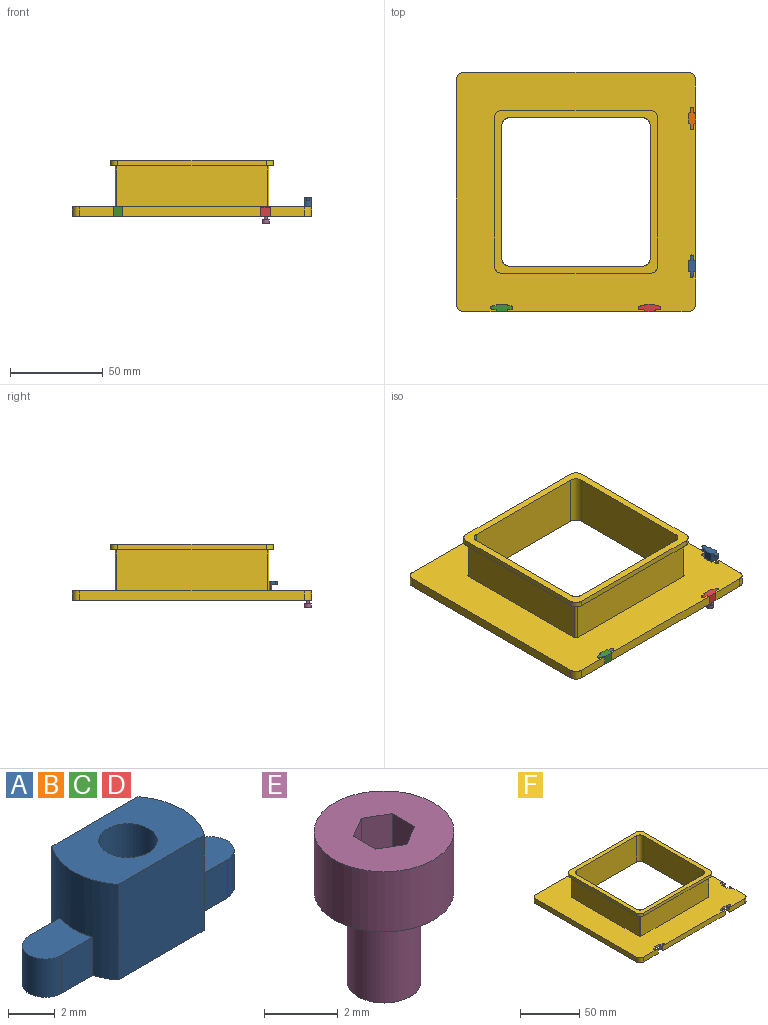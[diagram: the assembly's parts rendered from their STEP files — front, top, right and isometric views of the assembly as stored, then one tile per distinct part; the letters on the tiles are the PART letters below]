
ASSEMBLY  parts=6 mates=5
PART A: 16 faces, bbox 12x4x5 mm
  f0: plane 2x1.88mm, normal (0,1,0), area 3.8mm2, adj f2,f3,f8,f9
  f1: plane 2x1.88mm, normal (0,-1,0), area 3.8mm2, adj f2,f3,f8,f9
  f2: plane 2.88x2mm, normal (0,0,1), area 5.1mm2, adj f0,f1,f3,f9
  f3: cylinder r=1mm len=2mm, axis (0,0,-1), area 6.3mm2, adj f0,f1,f2,f8
  f4: plane 2x1.88mm, normal (0,1,0), area 3.8mm2, adj f5,f7,f8,f10
  f5: cylinder r=1mm len=2mm, axis (0,0,-1), area 6.3mm2, adj f4,f6,f7,f8
  f6: plane 2x1.88mm, normal (0,-1,0), area 3.8mm2, adj f5,f7,f8,f10
  f7: plane 2.88x2mm, normal (0,0,1), area 5.1mm2, adj f4,f5,f6,f10
  f8: plane 12x4mm, normal (0,0,-1), area 34.7mm2, adj f0,f1,f3,f4,f5,f6,f9,f10
  f9: cylinder r=3.28mm len=5mm, axis (0,0,-1), area 17.4mm2, adj f0,f1,f2,f8,f11,f12,f13
  f10: cylinder r=3.28mm len=5mm, axis (0,0,-1), area 17.4mm2, adj f4,f6,f7,f8,f11,f12,f13
  f11: plane 5.2x5mm, normal (0,1,0), area 26mm2, adj f8,f9,f10,f13
  f12: plane 5.2x5mm, normal (0,-1,0), area 26mm2, adj f8,f9,f10,f13
  f13: plane 6.56x4mm, normal (0,0,1), area 19.6mm2, adj f9,f10,f11,f12,f14
  f14: cylinder r=1.25mm len=4mm, axis (0,0,1), area 31.4mm2, adj f13,f15
  f15: plane 2.5x2.5mm, normal (0,0,1), area 4.9mm2, adj f14
PART B: same geometry as A
PART C: same geometry as A
PART D: same geometry as A
PART E: 12 faces, bbox 3.8x3.8x5 mm
  f0: plane 2x0.75mm, normal (-0.5,-0.87,0), area 1.7mm2, adj f1,f6,f7,f11
  f1: plane 2x0.87mm, normal (-1,0,0), area 1.7mm2, adj f0,f2,f7,f11
  f2: plane 2x0.75mm, normal (-0.5,0.87,0), area 1.7mm2, adj f1,f3,f7,f11
  f3: plane 2x0.75mm, normal (0.5,0.87,0), area 1.7mm2, adj f2,f4,f7,f11
  f4: plane 2x0.87mm, normal (1,0,0), area 1.7mm2, adj f3,f6,f7,f11
  f5: cylinder r=1.9mm len=3.8mm, axis (0,0,-1), area 23.9mm2, adj f7,f8
  f6: plane 2x0.75mm, normal (0.5,-0.87,0), area 1.7mm2, adj f0,f4,f7,f11
  f7: plane 3.8x3.8mm, normal (0,0,1), area 9.4mm2, adj f0,f1,f2,f3,f4,f5,f6
  f8: plane 3.8x3.8mm, normal (0,0,-1), area 8.2mm2, adj f5,f10
  f9: plane 2x2mm, normal (0,0,-1), area 3.1mm2, adj f10
  f10: cylinder r=1mm len=3mm, axis (0,0,1), area 18.8mm2, adj f8,f9
  f11: plane 1.73x1.5mm, normal (0,0,1), area 1.9mm2, adj f0,f1,f2,f3,f4,f6
PART F: 100 faces, bbox 129x129x30.2 mm
  f0: plane 129x129mm, normal (0,0,1), area 9600.2mm2, adj f1,f2,f5,f6,f7,f10,f11,f12
  f1: cylinder r=3.28mm len=5.1mm, axis (0,0,1), area 17.7mm2, adj f0,f3,f4,f30,f91,f96,f97,f98
  f2: cylinder r=3.28mm len=5.1mm, axis (0,0,1), area 17.7mm2, adj f0,f5,f8,f9,f91,f92,f93,f94
  f3: plane 14.2x3mm, normal (-1,0,0), area 42.6mm2, adj f1,f4,f38,f51
  f4: plane 129x129mm, normal (0,0,-1), area 1156.7mm2, adj f1,f3,f17,f30,f31,f32,f33,f35
  f5: plane 74.5x5.1mm, normal (1,0,0), area 379.9mm2, adj f0,f2,f6,f9
  f6: cylinder r=3.28mm len=5.1mm, axis (0,0,1), area 17.7mm2, adj f0,f5,f8,f9,f82,f87,f88,f89
  f7: cylinder r=3.28mm len=5.1mm, axis (0,0,1), area 17.7mm2, adj f0,f10,f24,f34,f82,f83,f84,f85
  f8: plane 74.5x3mm, normal (-1,0,0), area 223.5mm2, adj f2,f6,f9,f38
  f9: plane 74.5x4mm, normal (0,0,-1), area 294.3mm2, adj f2,f5,f6,f8
  f10: plane 17.9x5.1mm, normal (1,0,0), area 91.3mm2, adj f0,f7,f24,f59
  f11: cylinder r=3.28mm len=5.1mm, axis (0,0,-1), area 17.7mm2, adj f0,f13,f14,f24,f73,f78,f80,f81
  f12: cylinder r=3.28mm len=5.1mm, axis (0,0,-1), area 17.7mm2, adj f0,f15,f18,f19,f73,f74,f75,f76
  f13: plane 18.2x5.1mm, normal (0,-1,0), area 92.8mm2, adj f0,f11,f24,f59
  f14: plane 14.2x3mm, normal (0,1,0), area 42.6mm2, adj f11,f24,f38,f48
  f15: plane 74.5x4mm, normal (0,0,-1), area 294.3mm2, adj f12,f16,f18,f19
  f16: cylinder r=3.28mm len=5.1mm, axis (0,0,-1), area 17.7mm2, adj f0,f15,f18,f19,f64,f69,f71,f72
  f17: cylinder r=3.28mm len=5.1mm, axis (0,0,-1), area 17.7mm2, adj f0,f4,f33,f35,f64,f65,f66,f67
  f18: plane 74.5x5.1mm, normal (0,-1,0), area 380mm2, adj f0,f12,f15,f16
  f19: plane 74.5x3mm, normal (0,1,0), area 223.5mm2, adj f12,f15,f16,f38
  f20: plane 81x22.1mm, normal (0,-1,0), area 1790.1mm2, adj f0,f43,f62,f63
  f21: plane 81x22.1mm, normal (-1,0,0), area 1790.1mm2, adj f0,f43,f61,f62
  f22: plane 81x22.1mm, normal (0,1,0), area 1790.1mm2, adj f0,f43,f60,f61
  f23: plane 81x22.1mm, normal (1,0,0), area 1790.1mm2, adj f0,f43,f60,f63
  f24: plane 22.2x21.9mm, normal (0,0,-1), area 156.7mm2, adj f7,f10,f11,f13,f14,f34,f48,f59
  f25: plane 72x27.2mm, normal (0,1,0), area 1958.4mm2, adj f29,f38,f52,f55
  f26: plane 72x27.2mm, normal (-1,0,0), area 1958.4mm2, adj f29,f38,f52,f53
  f27: plane 72x27.2mm, normal (0,-1,0), area 1958.4mm2, adj f29,f38,f53,f54
  f28: plane 72x27.2mm, normal (1,0,0), area 1958.4mm2, adj f29,f38,f54,f55
  f29: plane 88x88mm, normal (0,0,1), area 1344mm2, adj f25,f26,f27,f28,f39,f40,f41,f42
  f30: plane 18.2x5.1mm, normal (1,0,0), area 92.8mm2, adj f0,f1,f4,f56
  f31: plane 121x5.1mm, normal (0,1,0), area 617.1mm2, adj f0,f4,f56,f57
  f32: plane 121x5.1mm, normal (-1,0,0), area 617.1mm2, adj f0,f4,f57,f58
  f33: plane 17.9x5.1mm, normal (0,-1,0), area 91.3mm2, adj f0,f4,f17,f58
  f34: plane 13.9x3mm, normal (-1,0,0), area 41.7mm2, adj f7,f24,f38,f48
  f35: plane 13.9x3mm, normal (0,1,0), area 41.7mm2, adj f4,f17,f38,f49
  f36: plane 113x3mm, normal (1,0,0), area 339mm2, adj f4,f38,f49,f50
  f37: plane 113x3mm, normal (0,-1,0), area 339mm2, adj f4,f38,f50,f51
  f38: plane 121x121mm, normal (0,0,-1), area 8241mm2, adj f3,f8,f14,f19,f25,f26,f27,f28
  f39: plane 80x3mm, normal (0,-1,0), area 240mm2, adj f29,f43,f44,f47
  f40: plane 80x3mm, normal (1,0,0), area 240mm2, adj f29,f43,f44,f45
  f41: plane 80x3mm, normal (0,1,0), area 240mm2, adj f29,f43,f45,f46
  f42: plane 80x3mm, normal (-1,0,0), area 240mm2, adj f29,f43,f46,f47
  f43: plane 88x88mm, normal (0,0,-1), area 842.1mm2, adj f20,f21,f22,f23,f39,f40,f41,f42
  f44: cylinder r=4mm len=4mm, axis (0,0,-1), area 18.8mm2, adj f29,f39,f40,f43
  f45: cylinder r=4mm len=4mm, axis (0,0,1), area 18.8mm2, adj f29,f40,f41,f43
  f46: cylinder r=4mm len=4mm, axis (0,0,-1), area 18.8mm2, adj f29,f41,f42,f43
  f47: cylinder r=4mm len=4mm, axis (0,0,1), area 18.8mm2, adj f29,f39,f42,f43
  f48: cylinder r=4mm len=4mm, axis (0,0,-1), area 18.8mm2, adj f14,f24,f34,f38
  f49: cylinder r=4mm len=4mm, axis (0,0,1), area 18.8mm2, adj f4,f35,f36,f38
  f50: cylinder r=4mm len=4mm, axis (0,0,-1), area 18.8mm2, adj f4,f36,f37,f38
  f51: cylinder r=4mm len=4mm, axis (0,0,1), area 18.8mm2, adj f3,f4,f37,f38
  f52: cylinder r=4mm len=27.2mm, axis (0,0,1), area 170.9mm2, adj f25,f26,f29,f38
  f53: cylinder r=4mm len=27.2mm, axis (0,0,-1), area 170.9mm2, adj f26,f27,f29,f38
  f54: cylinder r=4mm len=27.2mm, axis (0,0,1), area 170.9mm2, adj f27,f28,f29,f38
  f55: cylinder r=4mm len=27.2mm, axis (0,0,-1), area 170.9mm2, adj f25,f28,f29,f38
  f56: cylinder r=4mm len=5.1mm, axis (0,0,1), area 32mm2, adj f0,f4,f30,f31
  f57: cylinder r=4mm len=5.1mm, axis (0,0,-1), area 32mm2, adj f0,f4,f31,f32
  f58: cylinder r=4mm len=5.1mm, axis (0,0,1), area 32mm2, adj f0,f4,f32,f33
  f59: cylinder r=4mm len=5.1mm, axis (0,0,-1), area 32mm2, adj f0,f10,f13,f24
  f60: cylinder r=1mm len=22.1mm, axis (0,0,1), area 34.7mm2, adj f0,f22,f23,f43
  f61: cylinder r=1mm len=22.1mm, axis (0,0,-1), area 34.7mm2, adj f0,f21,f22,f43
  f62: cylinder r=1mm len=22.1mm, axis (0,0,1), area 34.7mm2, adj f0,f20,f21,f43
  f63: cylinder r=1mm len=22.1mm, axis (0,0,-1), area 34.7mm2, adj f0,f20,f23,f43
  f64: plane 5.2x2.1mm, normal (0,-1,0), area 10.9mm2, adj f0,f16,f17,f38
  f65: plane 2.88x2mm, normal (0,0,1), area 5.1mm2, adj f17,f66,f67,f68
  f66: plane 2.1x1.88mm, normal (0,-1,0), area 3.9mm2, adj f0,f17,f65,f68
  f67: plane 2.1x1.88mm, normal (0,1,0), area 3.9mm2, adj f0,f17,f65,f68
  f68: cylinder r=1mm len=2.1mm, axis (0,0,1), area 6.6mm2, adj f0,f65,f66,f67
  f69: plane 2.1x1.88mm, normal (0,1,0), area 3.9mm2, adj f0,f16,f70,f72
  f70: cylinder r=1mm len=2.1mm, axis (0,0,1), area 6.6mm2, adj f0,f69,f71,f72
  f71: plane 2.1x1.88mm, normal (0,-1,0), area 3.9mm2, adj f0,f16,f70,f72
  f72: plane 2.88x2mm, normal (0,0,1), area 5.1mm2, adj f16,f69,f70,f71
  f73: plane 5.2x2.1mm, normal (0,-1,0), area 10.9mm2, adj f0,f11,f12,f38
  f74: plane 2.88x2mm, normal (0,0,1), area 5.1mm2, adj f12,f75,f76,f77
  f75: plane 2.1x1.88mm, normal (0,-1,0), area 3.9mm2, adj f0,f12,f74,f77
  f76: plane 2.1x1.88mm, normal (0,1,0), area 3.9mm2, adj f0,f12,f74,f77
  f77: cylinder r=1mm len=2.1mm, axis (0,0,1), area 6.6mm2, adj f0,f74,f75,f76
  f78: plane 2.1x1.88mm, normal (0,1,0), area 3.9mm2, adj f0,f11,f79,f81
  f79: cylinder r=1mm len=2.1mm, axis (0,0,1), area 6.6mm2, adj f0,f78,f80,f81
  f80: plane 2.1x1.88mm, normal (0,-1,0), area 3.9mm2, adj f0,f11,f79,f81
  f81: plane 2.88x2mm, normal (0,0,1), area 5.1mm2, adj f11,f78,f79,f80
  f82: plane 5.2x2.1mm, normal (1,0,0), area 10.9mm2, adj f0,f6,f7,f38
  f83: plane 2.88x2mm, normal (0,0,1), area 5.1mm2, adj f7,f84,f85,f86
  f84: plane 2.1x1.88mm, normal (1,0,0), area 3.9mm2, adj f0,f7,f83,f86
  f85: plane 2.1x1.88mm, normal (-1,0,0), area 3.9mm2, adj f0,f7,f83,f86
  f86: cylinder r=1mm len=2.1mm, axis (0,0,1), area 6.6mm2, adj f0,f83,f84,f85
  f87: plane 2.1x1.88mm, normal (-1,0,0), area 3.9mm2, adj f0,f6,f89,f90
  f88: plane 2.1x1.88mm, normal (1,0,0), area 3.9mm2, adj f0,f6,f89,f90
  f89: plane 2.88x2mm, normal (0,0,1), area 5.1mm2, adj f6,f87,f88,f90
  f90: cylinder r=1mm len=2.1mm, axis (0,0,1), area 6.6mm2, adj f0,f87,f88,f89
  f91: plane 5.2x2.1mm, normal (1,0,0), area 10.9mm2, adj f0,f1,f2,f38
  f92: plane 2.88x2mm, normal (0,0,1), area 5.1mm2, adj f2,f93,f94,f95
  f93: plane 2.1x1.88mm, normal (1,0,0), area 3.9mm2, adj f0,f2,f92,f95
  f94: plane 2.1x1.88mm, normal (-1,0,0), area 3.9mm2, adj f0,f2,f92,f95
  f95: cylinder r=1mm len=2.1mm, axis (0,0,1), area 6.6mm2, adj f0,f92,f93,f94
  f96: plane 2.1x1.88mm, normal (-1,0,0), area 3.9mm2, adj f0,f1,f98,f99
  f97: plane 2.1x1.88mm, normal (1,0,0), area 3.9mm2, adj f0,f1,f98,f99
  f98: plane 2.88x2mm, normal (0,0,1), area 5.1mm2, adj f1,f96,f97,f99
  f99: cylinder r=1mm len=2.1mm, axis (0,0,1), area 6.6mm2, adj f0,f96,f97,f98
PLACE A rot(axis=(0.71,0.71,0),180deg) t=(64.84,-38.82,10.43)mm
PLACE B rot(axis=(0.71,0.71,0),180deg) t=(64.84,40.88,5.02)mm
PLACE C rot(axis=(1,0,0),180deg) t=(-37.66,-61.32,5.05)mm
PLACE D rot(axis=(1,0,0),180deg) t=(42.04,-61.32,5.01)mm
PLACE E rot(axis=(1,0,0),180deg) t=(42.04,-61.32,-1.95)mm
PLACE F t=(2.34,1.18,0)mm
MATE slider C.f14 <-> F.f16  axis (0,0,-1) through (-37.66,-61.32,4.05)mm
MATE slider A.f14 <-> F.f6  axis (0,0,-1) through (64.84,-38.82,5.43)mm
MATE slider B.f14 <-> F.f1  axis (0,0,-1) through (64.84,40.88,0.02)mm
MATE slider E.f5 <-> D.f14  axis (0,0,1) through (42.04,-61.32,1.05)mm
MATE slider D.f14 <-> F.f11  axis (0,0,-1) through (42.04,-61.32,4.01)mm
